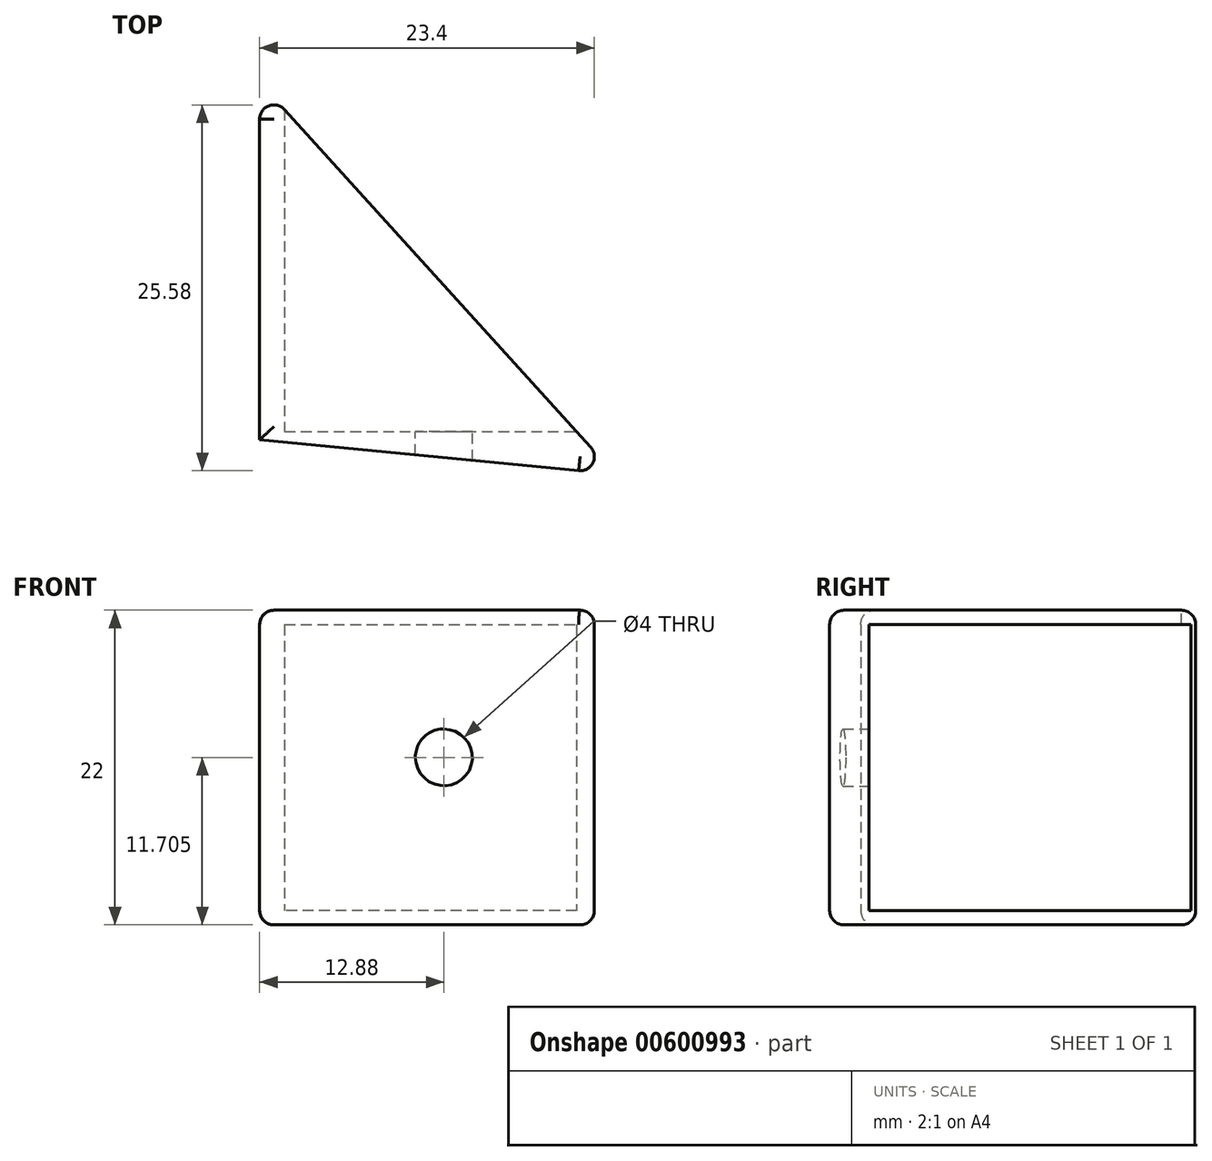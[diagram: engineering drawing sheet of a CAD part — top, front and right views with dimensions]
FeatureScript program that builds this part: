
annotation { "Feature Type Name" : "Feature", "Feature Type Description" : "" }
export const myFeature = defineFeature(function(context is Context, id is Id, definition is map)
    precondition{}
    {
        {
            var Q0;
            Q0=qCreatedBy(makeId("Top.planeOp"),FACE);
            var sketch = newSketch(context, id + "F0", { "sketchPlane" : qUnion([Q0])});
            skLineSegment(sketch, "E0", {"start": v(0, 0) * mm, "end": v(-24.88, 2.42) * mm});
            skLineSegment(sketch, "E1", {"start": v(-24.88, 2.42) * mm, "end": v(-24.88, 27.42) * mm});
            skLineSegment(sketch, "E2", {"start": v(-24.88, 27.42) * mm, "end": v(0, 0) * mm});
            skSolve(sketch);
        }
        {
            var Q0;
            Q0=makeQuery(id+"F0.imprint","IMPRINT",FACE,{"disambiguationData":[TD([[makeQuery(id+"F0.imprint","IMPRINT",EDGE,{"derivedFrom":sQuery(id+"F0.wireOp",EDGE,"E0")}),-1.0]])]});
            extrude(context, id + "F1", {"entities" : qUnion([Q0]), "depth" : 22 * mm, "offsetDistance" : 25 * mm});
        }
        {
            var Q0;
            Q0=makeQuery(id+"F1.opExtrude","CAP_EDGE",EDGE,{"disambiguationData":[OSD([sQuery(id+"F0.wireOp",EDGE,"E1")])],"isStart":false});
            var Q1;
            Q1=makeQuery(id+"F1.opExtrude","CAP_EDGE",EDGE,{"disambiguationData":[OSD([sQuery(id+"F0.wireOp",EDGE,"E0")])],"isStart":false});
            fillet(context, id + "F2", {"entities" : qUnion([Q0, Q1]), "radius" : 1 * mm, "tangentPropagation" : true, "allowEdgeOverflow" : false});
        }
        {
            var Q0;
            Q0=makeQuery(id+"F1.opExtrude","CAP_EDGE",EDGE,{"disambiguationData":[OSD([sQuery(id+"F0.wireOp",EDGE,"E2")])],"isStart":false});
            fillet(context, id + "F3", {"entities" : qUnion([Q0]), "radius" : 1 * mm, "tangentPropagation" : true, "allowEdgeOverflow" : false});
        }
        {
            var Q0;
            Q0=makeQuery(id+"F1.opExtrude","CAP_EDGE",EDGE,{"disambiguationData":[OSD([sQuery(id+"F0.wireOp",EDGE,"E0")])],"isStart":true});
            fillet(context, id + "F4", {"entities" : qUnion([Q0]), "radius" : 1 * mm, "tangentPropagation" : true, "allowEdgeOverflow" : false});
        }
        {
            var Q0;
            Q0=qCreatedBy(makeId("Front.planeOp"),FACE);
            cPlane(context, id + "F5", {"entities" : qUnion([Q0]), "cplaneType" : CPlaneType.OFFSET, "offset" : 3 * mm, "oppositeDirection" : true, "width" : 150 * mm, "height" : 150 * mm});
        }
        {
            var Q0;
            Q0=qCreatedBy(id+"F5.planeOp",FACE);
            var sketch = newSketch(context, id + "F6", { "sketchPlane" : qUnion([Q0])});
            skLineSegment(sketch, "E3.0", {"start": v(-2.58, 1) * mm, "end": v(-2.58, 21) * mm});
            skLineSegment(sketch, "E4.0", {"start": v(-2.58, 21) * mm, "end": v(-24.88, 21) * mm});
            skLineSegment(sketch, "E5.0", {"start": v(-24.88, 1) * mm, "end": v(-2.58, 1) * mm});
            skLineSegment(sketch, "E6.0", {"start": v(-23.14, 1) * mm, "end": v(-23.14, 21) * mm});
            skSolve(sketch);
        }
        {
            var Q0;
            Q0 = qSketchRegion(id + "F6", true);
            extrude(context, id + "F7", {"entities" : qUnion([Q0]), "operationType" : NewBodyOperationType.REMOVE, "oppositeDirection" : true, "depth" : 25 * mm, "offsetDistance" : 25 * mm});
        }
        {
            var Q0;
            Q0=makeQuery(id+"F7.boolean.opBoolean","COPY",FACE,{"derivedFrom":makeQuery(id+"F7.opExtrude","CAP_FACE",FACE,{"disambiguationData":[OSD([sQuery(id+"F6.wireOp",EDGE,"E3.0"),sQuery(id+"F6.wireOp",EDGE,"E4.0"),sQuery(id+"F6.wireOp",EDGE,"E5.0"),sQuery(id+"F6.wireOp",EDGE,"E6.0")])],"isStart":true})});
            var sketch = newSketch(context, id + "F8", { "sketchPlane" : qUnion([Q0])});
            skPoint(sketch, "E7", {"position": v(12, 11.7) * mm});
            skSolve(sketch);
        }
        {
            var Q0;
            Q0=sQuery(id+"F8.wireOp",VERTEX,"E7");
            var Q1;
            Q1=makeQuery(id+"F1.opExtrude","SWEPT_BODY",BODY,{"disambiguationData":[OSD([sQuery(id+"F0.wireOp",EDGE,"E0"),sQuery(id+"F0.wireOp",EDGE,"E1"),sQuery(id+"F0.wireOp",EDGE,"E2")])]});
            hole(context, id + "F9", {"style" : HoleStyle.SIMPLE, "endStyle" : HoleEndStyle.THROUGH, "holeDiameter" : 4 * mm, "majorDiameter" : 5 * mm, "isTappedThrough" : true, "tappedDepth" : 12 * mm, "tapClearance" : 3, "locations" : qUnion([Q0]), "scope" : qUnion([Q1])});
        }
    });
